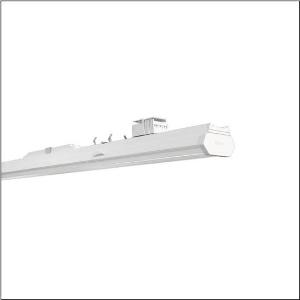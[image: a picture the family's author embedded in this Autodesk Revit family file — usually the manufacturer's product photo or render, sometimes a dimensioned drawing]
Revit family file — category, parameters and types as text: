
# Revit family: licross_11_protected_ho_51td1bdn6dxm
name_source: partatom
category: Lighting Fixtures
units: mm (PartAtom-declared; Revit-internal decimal feet)

## family parameters
Cut with Voids When Loaded = No
Host = Face
Light Source = No
Part Type = Normal
Room Calculation Point = No
Round Connector Dimension = Use Diameter
Shared = No

## types (1)
- --- (1 x LED, 13290 lm, 81.3 W, 6500K)
    Apparent Load = 81 VA
    CIE Flux Codes = 54 82 95 97 100
    Color Rendering = 80
    Color Temperature = 6500K
    Default Elevation = 1800 mm
    Description = Licross 11 Protected HO, luminaire insert, of sheet steel, galvanised, coil coated, white, length: 1.500mm, width: 90mm, height: 101mm, LED rated luminous flux: 13.290lm, light colour: 865, SDCM (Standard Deviation of Colour Matching)MacAdam ≤ 2 SDCM (initial), control gear: DALI 2, with plug, 5-pole, with phase selection, mains connection: 220..240V, AC, 50/60Hz, rated input power: 81W, internal wiring halogen-free, primary optical cover: cover, of PMMA, light emission: direct distribution, primary light characteristic: symmetric, protection rating (complete): IP54, insulation class (complete): insulation class I (protective earthing), certification: CE, ENEC, VDE, UKCA, protection symbol: D if used in an environment with non-conductive dust loads with corresponding accessories, impact resistance: IK06, permissible ambient temperature for indoor applications: -25..+35°C, corresponds to IFS (International Featured Standards) requirements for safety and quality in the food industry, reducing of maximum allowable ambient temperature of 5°C with ceiling mounting, LABS conformity tested according to VDMA 24364:2018-05, The light source and the operating device comply with the requirements of the Ecodesign Regulation (EU) 2019/2020 and are replaceable in accordance with this regulation, packaging unit: 1 piece
    Height = 92 mm
    Lamp = 1 x LED
    Lamp Light Flux = 13290 lm
    Lamp Power = 81.3 W
    Lamp count = 1
    Length = 1500 mm
    Luminous efficacy = 163 lm/W
    Manufacturer = Siteco
    ModVariant = No
    Model = 51TD1BDN6DXM
    Mounting Place = Ceiling
    Mounting Type = Pendant
    Number of Poles = 1
    OnlyDefault = Yes
    Power Factor = 1
    Product Name = Licross 11 Protected HO
    Product group = luminaire insert | ceiling pendant
    ProductGroupID = 901
    Protection Class = Protection class I
    Protection Degree = IP 54
    RLX_Detail_Level = 1
    RLX_Emergency_Light_Flux = 0 lm
    RLX_Emergency_Type = 0
    RLX_Emergency_Type_DB = No
    RlxData = <blob elided: 24709 chars, md5=9af7472a>
    Socket = socket
    Standby Power = 0 W
    System Light Flux = 13290 lm
    System Power = 81 W
    Type Comments = factory setting: luminous flux: 100 % | dim-lin: 254 | 550 mA
    Type Image = l_1256145.jpg
    URL = http://relux.com
    VarID = @adj_031503
    Voltage = 0 V
    Weight = 0.00 kg
    Width = 88 mm

## geometry (parser evidence)
native form markers: Blend x4, Sweep x9
no freeform markers — native parametric forms only
